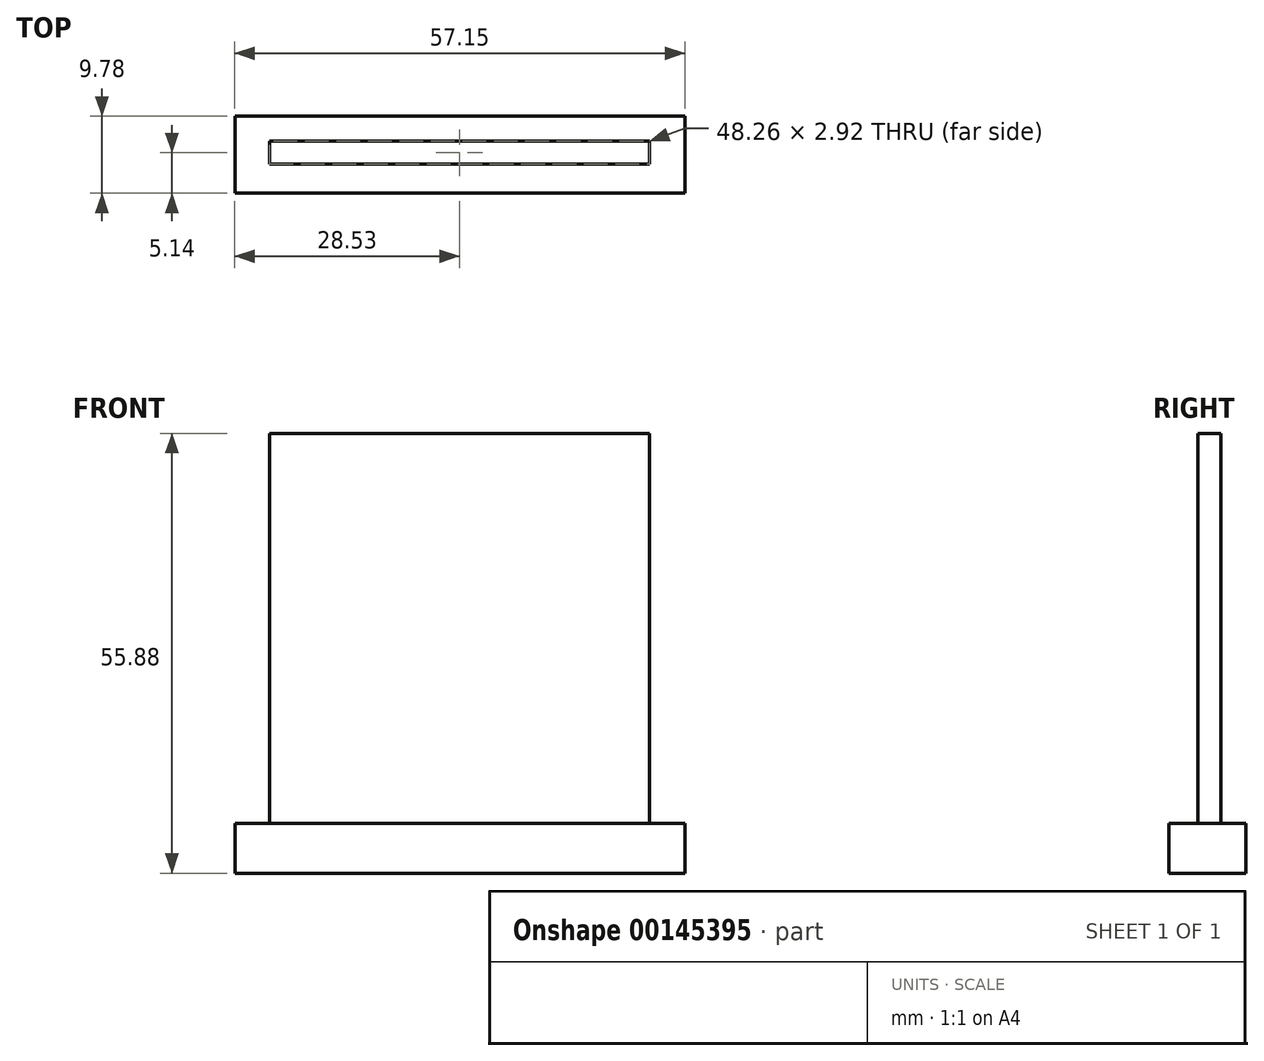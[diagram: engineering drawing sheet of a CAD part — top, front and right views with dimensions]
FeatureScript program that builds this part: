
annotation { "Feature Type Name" : "Feature", "Feature Type Description" : "" }
export const myFeature = defineFeature(function(context is Context, id is Id, definition is map)
    precondition{}
    {
        {
            var Q0;
            Q0=qCreatedBy(makeId("Top.planeOp"),FACE);
            var sketch = newSketch(context, id + "F0", { "sketchPlane" : qUnion([Q0])});
            skLineSegment(sketch, "E0.bottom", {"start": v(24.13, -1.46) * mm, "end": v(-24.13, -1.46) * mm});
            skLineSegment(sketch, "E0.top", {"start": v(24.13, 1.46) * mm, "end": v(-24.13, 1.46) * mm});
            skLineSegment(sketch, "E0.left", {"start": v(24.13, -1.46) * mm, "end": v(24.13, 1.46) * mm});
            skLineSegment(sketch, "E0.right", {"start": v(-24.13, -1.46) * mm, "end": v(-24.13, 1.46) * mm});
            skPoint(sketch, "E0.middle", {"position": v(0, 0) * mm});
            skLineSegment(sketch, "E1.0", {"start": v(28.62, 4.64) * mm, "end": v(-28.53, 4.64) * mm});
            skLineSegment(sketch, "E1.1", {"start": v(28.62, -5.14) * mm, "end": v(28.62, 4.64) * mm});
            skLineSegment(sketch, "E1.2", {"start": v(28.62, -5.14) * mm, "end": v(-28.53, -5.14) * mm});
            skLineSegment(sketch, "E1.3", {"start": v(-28.53, -5.14) * mm, "end": v(-28.53, 4.64) * mm});
            skSolve(sketch);
        }
        {
            var Q0;
            Q0=makeQuery(id+"F0.imprint","IMPRINT",FACE,{"disambiguationData":[TD([[makeQuery(id+"F0.imprint","IMPRINT",EDGE,{"derivedFrom":sQuery(id+"F0.wireOp",EDGE,"E0.bottom")}),-1.0]])]});
            extrude(context, id + "F1", {"entities" : qUnion([Q0]), "depth" : 55.88 * mm});
        }
        {
            var Q0;
            Q0=makeQuery(id+"F0.imprint","IMPRINT",FACE,{"disambiguationData":[TD([[makeQuery(id+"F0.imprint","IMPRINT",EDGE,{"derivedFrom":sQuery(id+"F0.wireOp",EDGE,"E0.bottom")}),1.0]])]});
            extrude(context, id + "F2", {"entities" : qUnion([Q0]), "operationType" : NewBodyOperationType.ADD, "depth" : 6.35 * mm});
        }
        {
            var Q0;
            Q0=makeQuery(id+"F1.opExtrude","SWEPT_BODY",BODY,{"disambiguationData":[OSD([sQuery(id+"F0.wireOp",EDGE,"E0.bottom"),sQuery(id+"F0.wireOp",EDGE,"E0.top"),sQuery(id+"F0.wireOp",EDGE,"E0.left"),sQuery(id+"F0.wireOp",EDGE,"E0.right")])]});
            transform(context, id + "F3", {"entities" : qUnion([Q0]), "transformType" : TransformType.TRANSLATION_3D, "dx" : 0 * mm, "dy" : 0 * mm, "dz" : 0 * mm, "makeCopy" : true});
        }
    });
